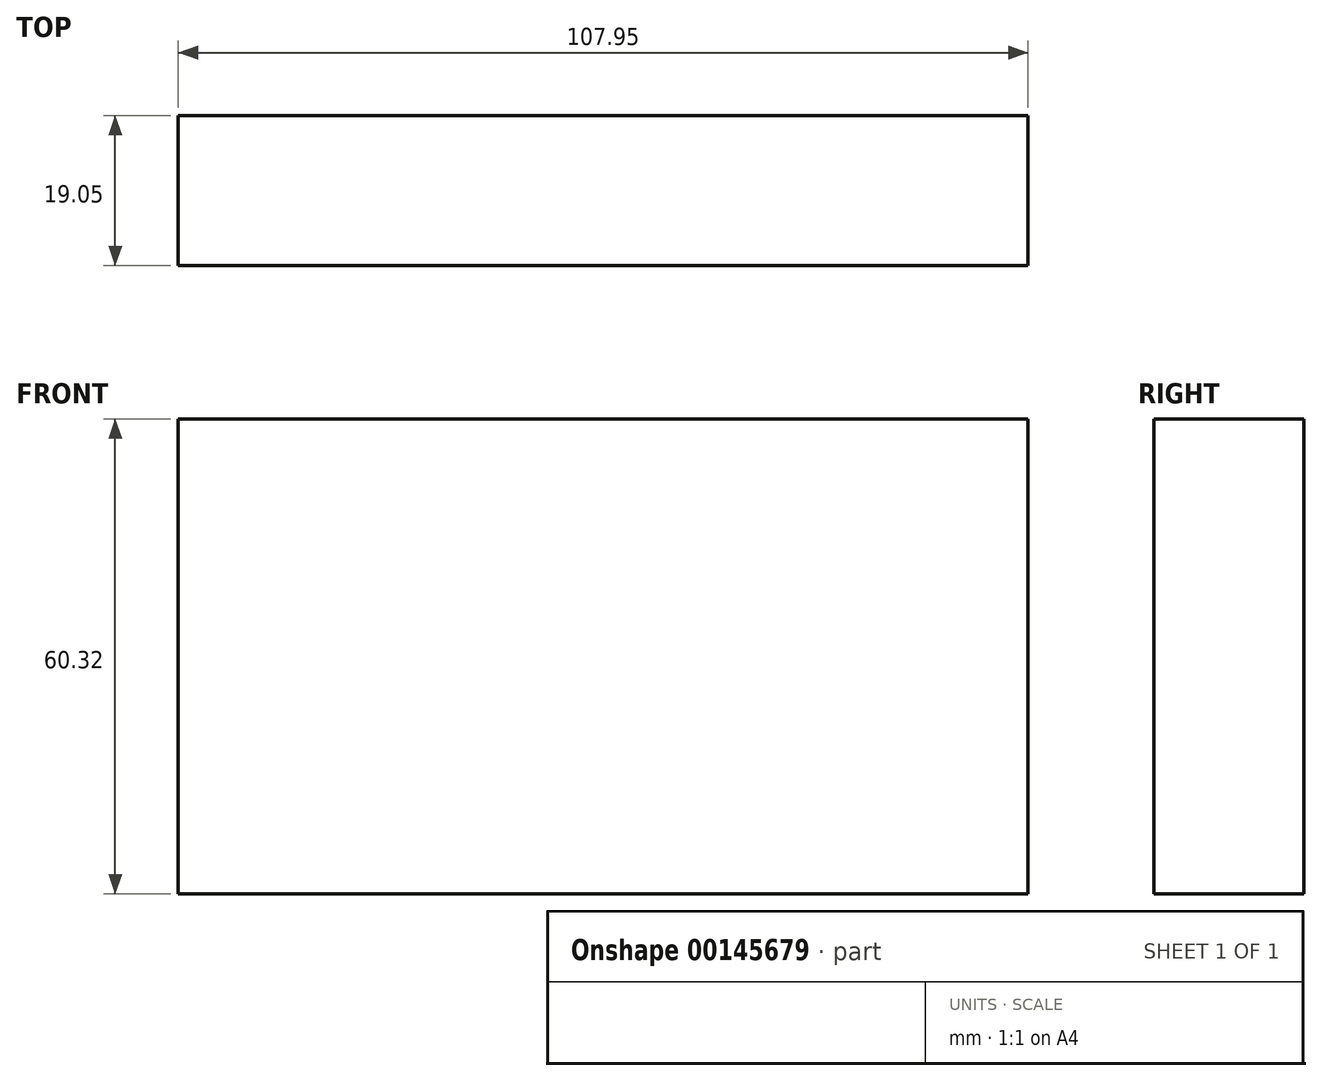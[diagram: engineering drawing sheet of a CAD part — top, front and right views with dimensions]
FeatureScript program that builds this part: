
annotation { "Feature Type Name" : "Feature", "Feature Type Description" : "" }
export const myFeature = defineFeature(function(context is Context, id is Id, definition is map)
    precondition{}
    {
        {
            var Q0;
            Q0=qCreatedBy(makeId("Top.planeOp"),FACE);
            var sketch = newSketch(context, id + "F0", { "sketchPlane" : qUnion([Q0])});
            skLineSegment(sketch, "E0.bottom", {"start": v(0, 0) * mm, "end": v(107.95, 0) * mm});
            skLineSegment(sketch, "E0.top", {"start": v(0, -19.05) * mm, "end": v(107.95, -19.05) * mm});
            skLineSegment(sketch, "E0.left", {"start": v(0, 0) * mm, "end": v(0, -19.05) * mm});
            skLineSegment(sketch, "E0.right", {"start": v(107.95, 0) * mm, "end": v(107.95, -19.05) * mm});
            skSolve(sketch);
        }
        {
            var Q0;
            Q0 = qSketchRegion(id + "F0", true);
            extrude(context, id + "F1", {"entities" : qUnion([Q0]), "depth" : 60.32 * mm});
        }
    });
